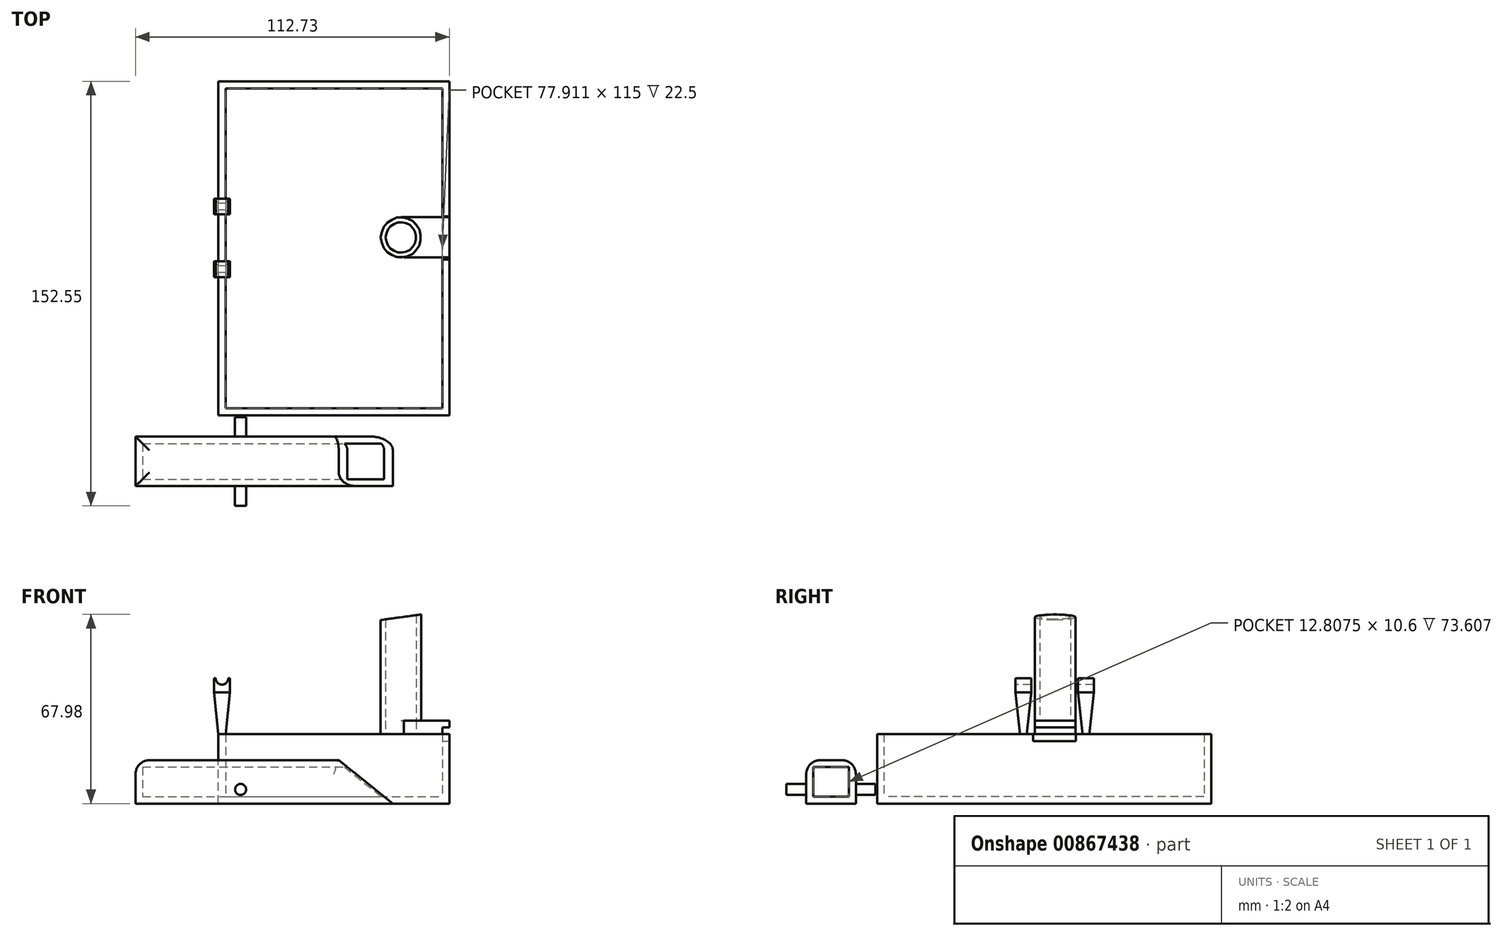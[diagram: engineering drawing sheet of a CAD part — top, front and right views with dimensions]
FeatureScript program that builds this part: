
annotation { "Feature Type Name" : "Feature", "Feature Type Description" : "" }
export const myFeature = defineFeature(function(context is Context, id is Id, definition is map)
    precondition{}
    {
        {
            var Q0;
            Q0=qCreatedBy(makeId("Top.planeOp"),FACE);
            var sketch = newSketch(context, id + "F0", { "sketchPlane" : qUnion([Q0])});
            skLineSegment(sketch, "E0.bottom", {"start": v(-71.57, 75.4) * mm, "end": v(48.43, 75.4) * mm});
            skLineSegment(sketch, "E0.top", {"start": v(-71.57, -44.6) * mm, "end": v(48.43, -44.6) * mm});
            skLineSegment(sketch, "E0.left", {"start": v(-71.57, 75.4) * mm, "end": v(-71.57, -44.6) * mm});
            skLineSegment(sketch, "E0.right", {"start": v(48.43, 75.4) * mm, "end": v(48.43, -44.6) * mm});
            skSolve(sketch);
        }
        {
            var Q0;
            Q0 = qSketchRegion(id + "F0", true);
            extrude(context, id + "F1", {"entities" : qUnion([Q0]), "depth" : 25 * mm, "offsetDistance" : 25 * mm});
        }
        {
            var Q0;
            Q0=makeQuery(id+"F1.opExtrude","CAP_FACE",FACE,{"disambiguationData":[OSD([sQuery(id+"F0.wireOp",EDGE,"E0.bottom"),sQuery(id+"F0.wireOp",EDGE,"E0.top"),sQuery(id+"F0.wireOp",EDGE,"E0.left"),sQuery(id+"F0.wireOp",EDGE,"E0.right")])],"isStart":false});
            shell(context, id + "F2", {"entities" : qUnion([Q0]), "thickness" : 2.5 * mm});
        }
        {
            var Q0;
            Q0=makeQuery(id+"F1.opExtrude","CAP_FACE",FACE,{"disambiguationData":[OSD([sQuery(id+"F0.wireOp",EDGE,"E0.bottom"),sQuery(id+"F0.wireOp",EDGE,"E0.top"),sQuery(id+"F0.wireOp",EDGE,"E0.left"),sQuery(id+"F0.wireOp",EDGE,"E0.right")])],"isStart":false});
            var sketch = newSketch(context, id + "F3", { "sketchPlane" : qUnion([Q0])});
            skCircle(sketch, "E1", {"center": v(31.03, 19.36) * mm, "radius": 5.52 * mm});
            skArc(sketch, "E2", {"start": v(31.07, 26.66) * mm, "mid": v(23.74, 18.87) * mm, "end": v(32.04, 12.13) * mm});
            skLineSegment(sketch, "E3.bottom", {"start": v(30.99, 26.66) * mm, "end": v(48.43, 26.66) * mm});
            skLineSegment(sketch, "E3.top", {"start": v(30.99, 12.13) * mm, "end": v(48.43, 12.13) * mm});
            skLineSegment(sketch, "E3.right", {"start": v(48.43, 26.66) * mm, "end": v(48.43, 12.13) * mm});
            skSolve(sketch);
        }
        {
            var Q0;
            Q0 = qSketchRegion(id + "F3", true);
            extrude(context, id + "F4", {"entities" : qUnion([Q0]), "operationType" : NewBodyOperationType.ADD, "depth" : 4.8 * mm, "offsetDistance" : 25 * mm});
        }
        {
            var Q0;
            Q0=makeQuery(id+"F4.opExtrude","CAP_FACE",FACE,{"disambiguationData":[OSD([sQuery(id+"F3.wireOp",EDGE,"E1"),sQuery(id+"F3.wireOp",EDGE,"E2"),sQuery(id+"F3.wireOp",EDGE,"E3.bottom"),sQuery(id+"F3.wireOp",EDGE,"E3.top"),sQuery(id+"F3.wireOp",EDGE,"E3.right")])],"isStart":false});
            var sketch = newSketch(context, id + "F5", { "sketchPlane" : qUnion([Q0])});
            skCircle(sketch, "E4", {"center": v(31.03, 19.36) * mm, "radius": 5.52 * mm});
            skCircle(sketch, "E5", {"center": v(31.03, 19.36) * mm, "radius": 7.3 * mm});
            skSolve(sketch);
        }
        {
            var Q0;
            Q0 = qSketchRegion(id + "F5", true);
            extrude(context, id + "F6", {"entities" : qUnion([Q0]), "operationType" : NewBodyOperationType.ADD, "depth" : 38.3 * mm, "offsetDistance" : 25 * mm});
        }
        {
            var Q0;
            Q0=makeQuery(id+"F1.opExtrude","CAP_FACE",FACE,{"disambiguationData":[OSD([sQuery(id+"F0.wireOp",EDGE,"E0.bottom"),sQuery(id+"F0.wireOp",EDGE,"E0.top"),sQuery(id+"F0.wireOp",EDGE,"E0.left"),sQuery(id+"F0.wireOp",EDGE,"E0.right")])],"isStart":false});
            var sketch = newSketch(context, id + "F7", { "sketchPlane" : qUnion([Q0])});
            skLineSegment(sketch, "E6.bottom", {"start": v(-71.57, 28.9) * mm, "end": v(-69.07, 28.9) * mm});
            skLineSegment(sketch, "E6.top", {"start": v(-71.57, 26.4) * mm, "end": v(-69.07, 26.4) * mm});
            skLineSegment(sketch, "E6.left", {"start": v(-71.57, 28.9) * mm, "end": v(-71.57, 26.4) * mm});
            skLineSegment(sketch, "E6.right", {"start": v(-69.07, 28.9) * mm, "end": v(-69.07, 26.4) * mm});
            skLineSegment(sketch, "E7.bottom", {"start": v(-71.57, 6.4) * mm, "end": v(-69.07, 6.4) * mm});
            skLineSegment(sketch, "E7.top", {"start": v(-71.57, 3.9) * mm, "end": v(-69.07, 3.9) * mm});
            skLineSegment(sketch, "E7.left", {"start": v(-71.57, 6.4) * mm, "end": v(-71.57, 3.9) * mm});
            skLineSegment(sketch, "E7.right", {"start": v(-69.07, 6.4) * mm, "end": v(-69.07, 3.9) * mm});
            skSolve(sketch);
        }
        {
            var Q0;
            Q0=makeQuery(id+"F7.imprint","IMPRINT",FACE,{"disambiguationData":[TD([[makeQuery(id+"F7.imprint","IMPRINT",EDGE,{"derivedFrom":sQuery(id+"F7.wireOp",EDGE,"E6.bottom")}),-1.0]])]});
            var Q1;
            Q1=makeQuery(id+"F7.imprint","IMPRINT",FACE,{"disambiguationData":[TD([[makeQuery(id+"F7.imprint","IMPRINT",EDGE,{"derivedFrom":sQuery(id+"F7.wireOp",EDGE,"E7.bottom")}),-1.0]])]});
            extrude(context, id + "F8", {"entities" : qUnion([Q0, Q1]), "operationType" : NewBodyOperationType.ADD, "depth" : 25 * mm, "offsetDistance" : 25 * mm, "hasDraft" : true, "draftAngle" : 6 * degree});
        }
        {
            var Q0;
            Q0=makeQuery(id+"F8.opExtrude","CAP_FACE",FACE,{"disambiguationData":[OSD([sQuery(id+"F7.wireOp",EDGE,"E7.bottom"),sQuery(id+"F7.wireOp",EDGE,"E7.top"),sQuery(id+"F7.wireOp",EDGE,"E7.left"),sQuery(id+"F7.wireOp",EDGE,"E7.right")])],"isStart":false});
            var sketch = newSketch(context, id + "F9", { "sketchPlane" : qUnion([Q0])});
            skLineSegment(sketch, "E8.bottom", {"start": v(-70.95, 9.02) * mm, "end": v(-70.03, 9.02) * mm});
            skLineSegment(sketch, "E8.top", {"start": v(-70.95, 1.26) * mm, "end": v(-70.03, 1.26) * mm});
            skLineSegment(sketch, "E8.left", {"start": v(-70.95, 9.02) * mm, "end": v(-70.95, 1.26) * mm});
            skLineSegment(sketch, "E8.right", {"start": v(-70.03, 9.02) * mm, "end": v(-70.03, 1.26) * mm});
            skSolve(sketch);
        }
        {
            var Q0;
            Q0 = qSketchRegion(id + "F9", true);
            extrude(context, id + "F10", {"entities" : qUnion([Q0]), "operationType" : NewBodyOperationType.ADD, "depth" : 1 * mm, "offsetDistance" : 25 * mm});
        }
        {
            var Q0;
            Q0=makeQuery(id+"F10.opExtrude","SWEPT_FACE",FACE,{"disambiguationData":[OSD([sQuery(id+"F9.wireOp",EDGE,"E8.top")])]});
            var sketch = newSketch(context, id + "F11", { "sketchPlane" : qUnion([Q0])});
            skCircle(sketch, "E9", {"center": v(-70.16, 50) * mm, "radius": 2.26 * mm});
            skSolve(sketch);
        }
        {
            var Q0;
            Q0=makeQuery(id+"F11.imprint","IMPRINT",FACE,{"disambiguationData":[TD([[makeQuery(id+"F11.imprint","IMPRINT",EDGE,{"derivedFrom":sQuery(id+"F11.wireOp",EDGE,"E9")}),1.0]])]});
            var Q1;
            {var subQ0=sQuery(id+"F9.wireOp",EDGE,"E8.top");Q1=makeQuery(id+"F11.imprint","IMPRINT",FACE,{"disambiguationData":[TD([[makeQuery(id+"F11.imprint","IMPRINT",EDGE,{"derivedFrom":makeQuery(id+"F10.opExtrude","CAP_EDGE",EDGE,{"disambiguationData":[OSD([subQ0])],"isStart":false})}),-1.0]])]});}
            extrude(context, id + "F12", {"entities" : qUnion([Q0, Q1]), "operationType" : NewBodyOperationType.REMOVE, "oppositeDirection" : true, "depth" : 42.5 * mm, "offsetDistance" : 25 * mm});
        }
        {
            var Q0;
            Q0=makeQuery(id+"F4.boolean.opBoolean","MERGE",FACE,{"derivedFrom":[makeQuery(id+"F1.opExtrude","SWEPT_FACE",FACE,{"disambiguationData":[OSD([sQuery(id+"F0.wireOp",EDGE,"E0.right")])]}),makeQuery(id+"F4.opExtrude","SWEPT_FACE",FACE,{"disambiguationData":[OSD([sQuery(id+"F3.wireOp",EDGE,"E3.right")])]})]});
            var sketch = newSketch(context, id + "F13", { "sketchPlane" : qUnion([Q0])});
            skLineSegment(sketch, "E10.bottom", {"start": v(12.13, 25) * mm, "end": v(26.66, 25) * mm});
            skLineSegment(sketch, "E10.top", {"start": v(12.13, 27.4) * mm, "end": v(26.66, 27.4) * mm});
            skLineSegment(sketch, "E10.left", {"start": v(12.13, 25) * mm, "end": v(12.13, 27.4) * mm});
            skLineSegment(sketch, "E10.right", {"start": v(26.66, 25) * mm, "end": v(26.66, 27.4) * mm});
            skSolve(sketch);
        }
        {
            var Q0;
            Q0 = qSketchRegion(id + "F13", true);
            extrude(context, id + "F14", {"entities" : qUnion([Q0]), "operationType" : NewBodyOperationType.REMOVE, "oppositeDirection" : true, "depth" : 2.5 * mm, "offsetDistance" : 25 * mm});
        }
        {
            var Q0;
            {var subQ1=sQuery(id+"F0.wireOp",EDGE,"E0.right");var subQ3=sQuery(id+"F0.wireOp",EDGE,"E0.bottom");Q0=makeQuery(id+"F14.boolean.opBoolean","SPLIT",FACE,{"disambiguationData":[TD([makeQuery(id+"F1.opExtrude","SWEPT_FACE",FACE,{"disambiguationData":[OSD([subQ3])]})])],"derivedFrom":makeQuery(id+"F4.boolean.opBoolean","MERGE",FACE,{"derivedFrom":[makeQuery(id+"F1.opExtrude","SWEPT_FACE",FACE,{"disambiguationData":[OSD([subQ1])]}),makeQuery(id+"F4.opExtrude","SWEPT_FACE",FACE,{"disambiguationData":[OSD([sQuery(id+"F3.wireOp",EDGE,"E3.right")])]})]})});}
            var sketch = newSketch(context, id + "F15", { "sketchPlane" : qUnion([Q0])});
            skLineSegment(sketch, "E11.bottom", {"start": v(11.43, 25) * mm, "end": v(26.89, 25) * mm});
            skLineSegment(sketch, "E11.top", {"start": v(11.43, 22.48) * mm, "end": v(26.89, 22.48) * mm});
            skLineSegment(sketch, "E11.left", {"start": v(11.43, 25) * mm, "end": v(11.43, 22.48) * mm});
            skLineSegment(sketch, "E11.right", {"start": v(26.89, 25) * mm, "end": v(26.89, 22.48) * mm});
            skSolve(sketch);
        }
        {
            var Q0;
            Q0 = qSketchRegion(id + "F15", true);
            extrude(context, id + "F16", {"entities" : qUnion([Q0]), "operationType" : NewBodyOperationType.REMOVE, "oppositeDirection" : true, "depth" : 2.5 * mm, "offsetDistance" : 25 * mm});
        }
        {
            var Q0;
            Q0=makeQuery(id+"F6.opExtrude","CAP_FACE",FACE,{"disambiguationData":[OSD([sQuery(id+"F5.wireOp",EDGE,"E4"),sQuery(id+"F5.wireOp",EDGE,"E5")])],"isStart":false});
            var sketch = newSketch(context, id + "F17", { "sketchPlane" : qUnion([Q0])});
            skLineSegment(sketch, "E12.bottom", {"start": v(30.7, 12.06) * mm, "end": v(31.7, 12.06) * mm});
            skLineSegment(sketch, "E12.top", {"start": v(30.7, 13.88) * mm, "end": v(31.7, 13.88) * mm});
            skLineSegment(sketch, "E12.left", {"start": v(30.7, 12.06) * mm, "end": v(30.7, 13.88) * mm});
            skLineSegment(sketch, "E12.right", {"start": v(31.7, 12.06) * mm, "end": v(31.7, 13.88) * mm});
            skSolve(sketch);
        }
        {
            var Q0;
            Q0 = qSketchRegion(id + "F17", true);
            extrude(context, id + "F18", {"entities" : qUnion([Q0]), "operationType" : NewBodyOperationType.ADD, "depth" : 1 * mm, "offsetDistance" : 25 * mm});
        }
        {
            var Q0;
            Q0=makeQuery(id+"F18.opExtrude","SWEPT_FACE",FACE,{"disambiguationData":[OSD([sQuery(id+"F17.wireOp",EDGE,"E12.bottom")])]});
            var sketch = newSketch(context, id + "F19", { "sketchPlane" : qUnion([Q0])});
            skLineSegment(sketch, "E13", {"start": v(39.2, 68.1) * mm, "end": v(20.18, 65.48) * mm});
            skLineSegment(sketch, "E14", {"start": v(20.18, 65.48) * mm, "end": v(21.17, 70.32) * mm});
            skLineSegment(sketch, "E15", {"start": v(21.17, 70.32) * mm, "end": v(41.08, 70.32) * mm});
            skLineSegment(sketch, "E16", {"start": v(41.08, 70.32) * mm, "end": v(39.2, 68.1) * mm});
            skSolve(sketch);
        }
        {
            var Q0;
            Q0 = qSketchRegion(id + "F19", true);
            extrude(context, id + "F20", {"entities" : qUnion([Q0]), "operationType" : NewBodyOperationType.REMOVE, "oppositeDirection" : true, "depth" : 25 * mm, "offsetDistance" : 25 * mm, "hasSecondDirection" : true, "secondDirectionOppositeDirection" : false, "secondDirectionDepth" : 25 * mm});
        }
        {
            var Q0;
            Q0=qCreatedBy(makeId("Top.planeOp"),FACE);
            var sketch = newSketch(context, id + "F21", { "sketchPlane" : qUnion([Q0])});
            skLineSegment(sketch, "E17.bottom", {"start": v(-64.3, -52.23) * mm, "end": v(28.15, -52.23) * mm});
            skLineSegment(sketch, "E17.top", {"start": v(-64.3, -70.04) * mm, "end": v(28.15, -70.04) * mm});
            skLineSegment(sketch, "E17.left", {"start": v(-64.3, -52.23) * mm, "end": v(-64.3, -70.04) * mm});
            skLineSegment(sketch, "E17.right", {"start": v(28.15, -52.23) * mm, "end": v(28.15, -70.04) * mm});
            skSolve(sketch);
        }
        {
            var Q0;
            Q0 = qSketchRegion(id + "F21", true);
            extrude(context, id + "F22", {"entities" : qUnion([Q0]), "depth" : 15.6 * mm, "offsetDistance" : 25 * mm});
        }
        {
            var Q0;
            Q0=makeQuery(id+"F22.opExtrude","SWEPT_FACE",FACE,{"disambiguationData":[OSD([sQuery(id+"F21.wireOp",EDGE,"E17.right")])]});
            shell(context, id + "F23", {"entities" : qUnion([Q0]), "thickness" : 2.5 * mm});
        }
        {
            var Q0;
            Q0=makeQuery(id+"F22.opExtrude","SWEPT_FACE",FACE,{"disambiguationData":[OSD([sQuery(id+"F21.wireOp",EDGE,"E17.top")])]});
            var sketch = newSketch(context, id + "F24", { "sketchPlane" : qUnion([Q0])});
            skLineSegment(sketch, "E18", {"start": v(28.15, 0) * mm, "end": v(8.68, 15.6) * mm});
            skLineSegment(sketch, "E19", {"start": v(8.68, 15.6) * mm, "end": v(28.15, 15.6) * mm});
            skLineSegment(sketch, "E20", {"start": v(28.15, 15.6) * mm, "end": v(28.15, 0) * mm});
            skSolve(sketch);
        }
        {
            var Q0;
            Q0 = qSketchRegion(id + "F24", true);
            extrude(context, id + "F25", {"entities" : qUnion([Q0]), "operationType" : NewBodyOperationType.REMOVE, "oppositeDirection" : true, "depth" : 20.5 * mm, "offsetDistance" : 25 * mm});
        }
        {
            var Q0;
            Q0=makeQuery(id+"F22.opExtrude","CAP_EDGE",EDGE,{"disambiguationData":[OSD([sQuery(id+"F21.wireOp",EDGE,"E17.top")])],"isStart":false});
            var Q1;
            Q1=makeQuery(id+"F22.opExtrude","CAP_EDGE",EDGE,{"disambiguationData":[OSD([sQuery(id+"F21.wireOp",EDGE,"E17.bottom")])],"isStart":false});
            var Q2;
            Q2=makeQuery(id+"F22.opExtrude","CAP_EDGE",EDGE,{"disambiguationData":[OSD([sQuery(id+"F21.wireOp",EDGE,"E17.left")])],"isStart":false});
            var Q3;
            Q3=makeQuery(id+"F25.boolean.opBoolean","COPY",EDGE,{"derivedFrom":makeQuery(id+"F25.opExtrude","CAP_EDGE",EDGE,{"disambiguationData":[OSD([sQuery(id+"F24.wireOp",EDGE,"E18")])],"isStart":true})});
            var Q4;
            Q4=makeQuery(id+"F25.boolean.opBoolean","INTERSECT",EDGE,{"derivedFrom":[makeQuery(id+"F22.opExtrude","SWEPT_FACE",FACE,{"disambiguationData":[OSD([sQuery(id+"F21.wireOp",EDGE,"E17.bottom")])]}),makeQuery(id+"F25.opExtrude","SWEPT_FACE",FACE,{"disambiguationData":[OSD([sQuery(id+"F24.wireOp",EDGE,"E18")])]})]});
            var Q5;
            Q5=makeQuery(id+"F25.boolean.opBoolean","COPY",EDGE,{"derivedFrom":makeQuery(id+"F25.opExtrude","SWEPT_EDGE",EDGE,{"disambiguationData":[OSD([sQuery(id+"F21.wireOp",EDGE,"E17.top"),sQuery(id+"F24.wireOp",EDGE,"E18"),sQuery(id+"F24.wireOp",EDGE,"E19")])]})});
            fillet(context, id + "F26", {"entities" : qUnion([Q0, Q1, Q2, Q3, Q4, Q5]), "radius" : 5 * mm, "tangentPropagation" : true, "allowEdgeOverflow" : false});
        }
        {
            var Q0;
            Q0=makeQuery(id+"F22.opExtrude","SWEPT_FACE",FACE,{"disambiguationData":[OSD([sQuery(id+"F21.wireOp",EDGE,"E17.top")])]});
            var sketch = newSketch(context, id + "F27", { "sketchPlane" : qUnion([Q0])});
            skCircle(sketch, "E21", {"center": v(-26.57, 5.07) * mm, "radius": 2 * mm});
            skSolve(sketch);
        }
        {
            var Q0;
            Q0 = qSketchRegion(id + "F27", true);
            extrude(context, id + "F28", {"entities" : qUnion([Q0]), "operationType" : NewBodyOperationType.ADD, "depth" : 7.1 * mm, "offsetDistance" : 25 * mm, "hasSecondDirection" : true, "secondDirectionOppositeDirection" : true, "secondDirectionDepth" : 24.8 * mm});
        }
        {
            var Q0;
            Q0=makeQuery(id+"F23.opShell","OFFSET_FACE",FACE,{"disambiguationData":[OSD([sQuery(id+"F21.wireOp",EDGE,"E17.left")])]});
            var sketch = newSketch(context, id + "F29", { "sketchPlane" : qUnion([Q0])});
            skLineSegment(sketch, "E22.bottom", {"start": v(-67.54, 13.1) * mm, "end": v(-54.73, 13.1) * mm});
            skLineSegment(sketch, "E22.top", {"start": v(-67.54, 2.5) * mm, "end": v(-54.73, 2.5) * mm});
            skLineSegment(sketch, "E22.left", {"start": v(-67.54, 13.1) * mm, "end": v(-67.54, 2.5) * mm});
            skLineSegment(sketch, "E22.right", {"start": v(-54.73, 13.1) * mm, "end": v(-54.73, 2.5) * mm});
            skSolve(sketch);
        }
        {
            var Q0;
            Q0 = qSketchRegion(id + "F29", true);
            extrude(context, id + "F30", {"entities" : qUnion([Q0]), "operationType" : NewBodyOperationType.REMOVE, "depth" : 120 * mm, "offsetDistance" : 25 * mm});
        }
        {
            var Q0;
            Q0=makeQuery(id+"F2.opShell","OFFSET_FACE",FACE,{"disambiguationData":[OSD([sQuery(id+"F0.wireOp",EDGE,"E0.bottom"),sQuery(id+"F0.wireOp",EDGE,"E0.top"),sQuery(id+"F0.wireOp",EDGE,"E0.left"),sQuery(id+"F0.wireOp",EDGE,"E0.right")])]});
            var sketch = newSketch(context, id + "F31", { "sketchPlane" : qUnion([Q0])});
            skLineSegment(sketch, "E23.bottom", {"start": v(-34.57, 77.3) * mm, "end": v(-82.18, 77.3) * mm});
            skLineSegment(sketch, "E23.top", {"start": v(-34.57, -49.3) * mm, "end": v(-82.18, -49.3) * mm});
            skLineSegment(sketch, "E23.left", {"start": v(-34.57, 77.3) * mm, "end": v(-34.57, -49.3) * mm});
            skLineSegment(sketch, "E23.right", {"start": v(-82.18, 77.3) * mm, "end": v(-82.18, -49.3) * mm});
            skSolve(sketch);
        }
        {
            var Q0;
            {var subQ5=sQuery(id+"F31.wireOp",EDGE,"E23.bottom");Q0=makeQuery(id+"F31.imprint","IMPRINT",FACE,{"disambiguationData":[TD([[makeQuery(id+"F31.imprint","IMPRINT",EDGE,{"derivedFrom":subQ5}),1.0]])]});}
            var Q1;
            {var subQ7=sQuery(id+"F0.wireOp",EDGE,"E0.left");var subQ8=makeQuery(id+"F2.opShell","OFFSET_EDGE",EDGE,{"disambiguationData":[OSD([subQ7]),TDD([makeQuery(id+"F1.opExtrude","CAP_EDGE",EDGE,{"disambiguationData":[OSD([subQ7])],"isStart":true})])]});Q1=makeQuery(id+"F31.imprint","IMPRINT",FACE,{"disambiguationData":[TD([[makeQuery(id+"F31.imprint","IMPRINT",EDGE,{"derivedFrom":subQ8}),1.0]])]});}
            extrude(context, id + "F32", {"entities" : qUnion([Q0, Q1]), "operationType" : NewBodyOperationType.REMOVE, "oppositeDirection" : true, "depth" : 25 * mm, "offsetDistance" : 25 * mm, "hasSecondDirection" : true, "secondDirectionOppositeDirection" : false, "secondDirectionDepth" : 53.7 * mm});
        }
        {
            var Q0;
            Q0=makeQuery(id+"F2.opShell","OFFSET_FACE",FACE,{"disambiguationData":[OSD([sQuery(id+"F0.wireOp",EDGE,"E0.bottom"),sQuery(id+"F0.wireOp",EDGE,"E0.top"),sQuery(id+"F0.wireOp",EDGE,"E0.left"),sQuery(id+"F0.wireOp",EDGE,"E0.right")])]});
            var sketch = newSketch(context, id + "F33", { "sketchPlane" : qUnion([Q0])});
            skLineSegment(sketch, "E24.bottom", {"start": v(-34.57, 72.9) * mm, "end": v(-31.98, 72.9) * mm});
            skLineSegment(sketch, "E24.top", {"start": v(-34.57, -42.1) * mm, "end": v(-31.98, -42.1) * mm});
            skLineSegment(sketch, "E24.left", {"start": v(-34.57, 72.9) * mm, "end": v(-34.57, -42.1) * mm});
            skLineSegment(sketch, "E24.right", {"start": v(-31.98, 72.9) * mm, "end": v(-31.98, -42.1) * mm});
            skSolve(sketch);
        }
        {
            var Q0;
            Q0 = qSketchRegion(id + "F33", true);
            extrude(context, id + "F34", {"entities" : qUnion([Q0]), "operationType" : NewBodyOperationType.ADD, "depth" : 22.5 * mm, "offsetDistance" : 25 * mm});
        }
        {
            var Q0;
            {var subQ3=sQuery(id+"F0.wireOp",EDGE,"E0.right");var subQ5=sQuery(id+"F0.wireOp",EDGE,"E0.left");var subQ8=sQuery(id+"F0.wireOp",EDGE,"E0.top");var subQ9=makeQuery(id+"F1.opExtrude","SWEPT_FACE",FACE,{"disambiguationData":[OSD([subQ8])]});var subQ17=sQuery(id+"F0.wireOp",EDGE,"E0.bottom");var subQ18=makeQuery(id+"F1.opExtrude","CAP_FACE",FACE,{"disambiguationData":[OSD([subQ17,subQ8,subQ5,subQ3])],"isStart":false});var subQ19=makeQuery(id+"F1.opExtrude","SWEPT_FACE",FACE,{"disambiguationData":[OSD([subQ17])]});var subQ24=makeQuery(id+"F14.boolean.opBoolean","MERGE",FACE,{"derivedFrom":[makeQuery(id+"F8.boolean.opBoolean","SPLIT",FACE,{"disambiguationData":[TD([subQ19])],"derivedFrom":subQ18}),makeQuery(id+"F8.boolean.opBoolean","SPLIT",FACE,{"disambiguationData":[TD([subQ9])],"derivedFrom":subQ18}),makeQuery(id+"F14.opExtrude","SWEPT_FACE",FACE,{"disambiguationData":[OSD([sQuery(id+"F13.wireOp",EDGE,"E10.bottom")])]})]});Q0=makeQuery(id+"F34.boolean.opBoolean","MERGE",FACE,{"derivedFrom":[makeQuery(id+"F16.boolean.opBoolean","SPLIT",FACE,{"disambiguationData":[TD([subQ19])],"derivedFrom":subQ24}),makeQuery(id+"F16.boolean.opBoolean","SPLIT",FACE,{"disambiguationData":[TD([subQ9])],"derivedFrom":subQ24}),makeQuery(id+"F34.opExtrude","CAP_FACE",FACE,{"disambiguationData":[OSD([sQuery(id+"F33.wireOp",EDGE,"E24.bottom"),sQuery(id+"F33.wireOp",EDGE,"E24.top"),sQuery(id+"F33.wireOp",EDGE,"E24.left"),sQuery(id+"F33.wireOp",EDGE,"E24.right")])],"isStart":false})]});}
            var sketch = newSketch(context, id + "F35", { "sketchPlane" : qUnion([Q0])});
            skLineSegment(sketch, "E25.bottom", {"start": v(-32.75, -51.3) * mm, "end": v(-30.56, -51.3) * mm});
            skLineSegment(sketch, "E25.top", {"start": v(-32.75, -71.2) * mm, "end": v(-30.56, -71.2) * mm});
            skLineSegment(sketch, "E25.left", {"start": v(-32.75, -51.3) * mm, "end": v(-32.75, -71.2) * mm});
            skLineSegment(sketch, "E25.right", {"start": v(-30.56, -51.3) * mm, "end": v(-30.56, -71.2) * mm});
            skLineSegment(sketch, "E26.bottom", {"start": v(-34.57, 29.2) * mm, "end": v(-31.98, 29.2) * mm});
            skLineSegment(sketch, "E26.top", {"start": v(-34.57, 31.7) * mm, "end": v(-31.98, 31.7) * mm});
            skLineSegment(sketch, "E26.left", {"start": v(-34.57, 29.2) * mm, "end": v(-34.57, 31.7) * mm});
            skLineSegment(sketch, "E26.right", {"start": v(-31.98, 29.2) * mm, "end": v(-31.98, 31.7) * mm});
            skLineSegment(sketch, "E27.bottom", {"start": v(-34.57, 9.2) * mm, "end": v(-31.98, 9.2) * mm});
            skLineSegment(sketch, "E27.top", {"start": v(-34.57, 6.7) * mm, "end": v(-31.98, 6.7) * mm});
            skLineSegment(sketch, "E27.left", {"start": v(-34.57, 9.2) * mm, "end": v(-34.57, 6.7) * mm});
            skLineSegment(sketch, "E27.right", {"start": v(-31.98, 9.2) * mm, "end": v(-31.98, 6.7) * mm});
            skSolve(sketch);
        }
        {
            var Q0;
            Q0=makeQuery(id+"F35.imprint","IMPRINT",FACE,{"disambiguationData":[TD([[makeQuery(id+"F35.imprint","IMPRINT",EDGE,{"derivedFrom":sQuery(id+"F35.wireOp",EDGE,"E27.bottom")}),-1.0]])]});
            var Q1;
            Q1=makeQuery(id+"F35.imprint","IMPRINT",FACE,{"disambiguationData":[TD([[makeQuery(id+"F35.imprint","IMPRINT",EDGE,{"derivedFrom":sQuery(id+"F35.wireOp",EDGE,"E26.bottom")}),1.0]])]});
            extrude(context, id + "F36", {"entities" : qUnion([Q0, Q1]), "operationType" : NewBodyOperationType.ADD, "depth" : 15 * mm, "offsetDistance" : 25 * mm, "hasDraft" : true, "draftAngle" : 6 * degree});
        }
        {
            var Q0;
            Q0=makeQuery(id+"F36.opExtrude","CAP_FACE",FACE,{"disambiguationData":[OSD([sQuery(id+"F35.wireOp",EDGE,"E26.bottom"),sQuery(id+"F35.wireOp",EDGE,"E26.top"),sQuery(id+"F35.wireOp",EDGE,"E26.left"),sQuery(id+"F35.wireOp",EDGE,"E26.right")])],"isStart":false});
            var sketch = newSketch(context, id + "F37", { "sketchPlane" : qUnion([Q0])});
            skLineSegment(sketch, "E28.bottom", {"start": v(-36.15, 33.28) * mm, "end": v(-30.4, 33.28) * mm});
            skLineSegment(sketch, "E28.top", {"start": v(-36.15, 27.63) * mm, "end": v(-30.4, 27.63) * mm});
            skLineSegment(sketch, "E28.left", {"start": v(-36.15, 33.28) * mm, "end": v(-36.15, 27.63) * mm});
            skLineSegment(sketch, "E28.right", {"start": v(-30.4, 33.28) * mm, "end": v(-30.4, 27.63) * mm});
            skLineSegment(sketch, "E29.bottom", {"start": v(-36.15, 10.8) * mm, "end": v(-30.4, 10.8) * mm});
            skLineSegment(sketch, "E29.top", {"start": v(-36.15, 5.12) * mm, "end": v(-30.4, 5.12) * mm});
            skLineSegment(sketch, "E29.left", {"start": v(-36.15, 10.8) * mm, "end": v(-36.15, 5.12) * mm});
            skLineSegment(sketch, "E29.right", {"start": v(-30.4, 10.8) * mm, "end": v(-30.4, 5.12) * mm});
            skSolve(sketch);
        }
        {
            var Q0;
            Q0 = qSketchRegion(id + "F37", true);
            extrude(context, id + "F38", {"entities" : qUnion([Q0]), "operationType" : NewBodyOperationType.ADD, "depth" : 5 * mm, "offsetDistance" : 25 * mm});
        }
        {
            var Q0;
            Q0=makeQuery(id+"F38.opExtrude","SWEPT_FACE",FACE,{"disambiguationData":[OSD([sQuery(id+"F37.wireOp",EDGE,"E29.top")])]});
            var sketch = newSketch(context, id + "F39", { "sketchPlane" : qUnion([Q0])});
            skCircle(sketch, "E30", {"center": v(-33.28, 45) * mm, "radius": 2.24 * mm});
            skSolve(sketch);
        }
        {
            var Q0;
            Q0 = qSketchRegion(id + "F39", true);
            extrude(context, id + "F40", {"entities" : qUnion([Q0]), "operationType" : NewBodyOperationType.REMOVE, "oppositeDirection" : true, "depth" : 38.6 * mm, "offsetDistance" : 25 * mm});
        }
    });
